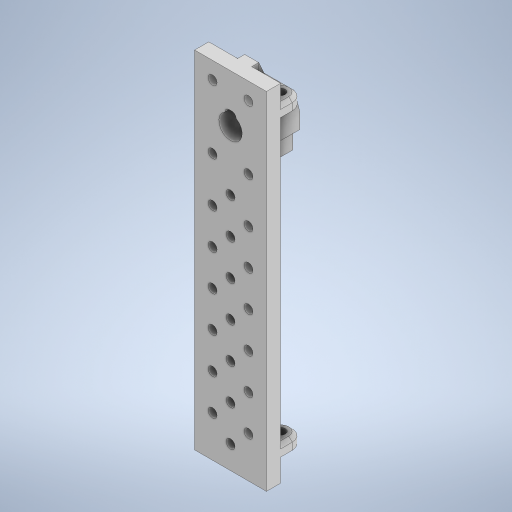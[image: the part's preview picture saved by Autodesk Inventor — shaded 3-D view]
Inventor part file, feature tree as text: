
AUTODESK INVENTOR PART (.ipt)
format: ipt  version: 2024 (Build 280153000, 153)  size: 1,184,256 bytes
history: native  units: mm
features: projected_geometry x30, extrude x22, sketch x18, plane x4, mirror x2, other x2, chamfer x1, loft x1
ambient origin geometry x8: Origin, YZ Plane, XZ Plane, XY Plane, X Axis, Y Axis, Z Axis, Center Point
bodies: Solid1 (feature_tree)
feature tree (80):
  extrude  "Extrusion1"  Depth=10.0mm
  extrude  "Extrusion2"  Depth=16.002mm
  extrude  "Extrusion3"  Depth=16.002mm
  plane  "Work Plane5"
  mirror  "Mirror1"
  extrude  "Extrusion4"  Depth=5.5118mm
  extrude  "Extrusion22"  Depth=2.9972mm
  extrude  "Extrusion23"  Depth=8.001mm
  extrude  "Extrusion24"  Depth=152.5mm
  extrude  "Extrusion14"  Depth=215.0mm
  plane  "Work Plane2"
  extrude  "Extrusion25"  Depth=8.25mm
  chamfer  "Chamfer1"  Distance=1.0mm
  plane  "Work Plane3"
  loft  "Loft6"
  extrude  "Extrusion27"  Depth=10.0mm
  extrude  "Extrusion28"  Depth=10.0mm
  extrude  "Extrusion29"  Depth=10.0mm
  plane  "Work Plane4"
  extrude  "Extrusion30"  Depth=10.0mm
  extrude  "Extrusion31"  Depth=10.0mm
  extrude  "Extrusion32"  Depth=10.0mm
  extrude  "Extrusion33"  Depth=10.0mm
  extrude  "Extrusion34"  Depth=10.0mm
  mirror  "Mirror2"
  extrude  "Extrusion35"  Depth=10.0mm
  extrude  "Extrusion36"  Depth=10.0mm
  extrude  "Extrusion37"  Depth=10.0mm
  sketch  "Sketch40"  dims[d25=1.0mm]
  extrude  "Extrusion38"  Depth=10.0mm
  extrude  "Extrusion39"  Depth=3.0mm
  sketch  "Sketch1"  dims[d0=5.0mm d1=10.0mm]
  projected_geometry  "Projected Loop1"
  projected_geometry  "Projected Loop2"
  projected_geometry  "Projected Loop3"
  projected_geometry  "Projected Loop17"
  sketch  "Sketch23"  dims[d2=122.8852mm d3=16.002mm]
  projected_geometry  "Projected Loop30"
  sketch  "Sketch24"  dims[d4=2.9972mm d5=16.002mm]
  projected_geometry  "Projected Loop31"
  sketch  "Sketch25"  dims[d6=11.938mm d7=5.5118mm]
  projected_geometry  "Projected Loop32"
  sketch  "Sketch26"  dims[d8=5.0038mm d9=2.9972mm]
  projected_geometry  "Projected Loop33"
  other  "Edges11"
  other  "Edges12"
  sketch  "Sketch29"  dims[d10=6.096mm d11=8.001mm]
  projected_geometry  "Projected Loop41"
  projected_geometry  "Projected Loop42"
  projected_geometry  "Projected Loop43"
  projected_geometry  "Projected Loop44"
  projected_geometry  "Projected Loop45"
  projected_geometry  "Projected Loop46"
  sketch  "Sketch30"  dims[d12=6.5mm d13=152.5mm]
  projected_geometry  "Projected Loop47"
  sketch  "Sketch31"  dims[d14=60.0mm d15=215.0mm]
  projected_geometry  "Projected Loop48"
  sketch  "Sketch32"  dims[d16=50.8mm d17=8.25mm]
  projected_geometry  "Projected Loop49"
  sketch  "Sketch33"  dims[d18=16.5mm]
  sketch  "Sketch34"  dims[d19=25.4mm]
  projected_geometry  "Projected Loop50"
  sketch  "Sketch35"  dims[d20=6.35mm]
  projected_geometry  "Projected Loop51"
  sketch  "Sketch36"  dims[d21=127.8852mm]
  projected_geometry  "Projected Loop52"
  sketch  "Sketch37"  dims[d22=10.0076mm]
  projected_geometry  "Projected Loop53"
  projected_geometry  "Projected Loop54"
  sketch  "Sketch38"  dims[d23=20.0mm]
  projected_geometry  "Projected Loop55"
  projected_geometry  "Projected Loop56"
  projected_geometry  "Projected Loop57"
  sketch  "Sketch39"  dims[d24=1.0mm]
  projected_geometry  "Projected Loop58"
  projected_geometry  "Projected Loop59"
  projected_geometry  "Projected Loop60"
  sketch  "Sketch41"  dims[d26=1.0mm d27=1.0mm d28=1.0mm d29=1.0mm d30=1.0mm d31=1.0mm d32=1.0mm d33=1.0mm d34=1.0mm d35=1.0mm d36=1.0mm d37=1.0mm d38=1.0mm d39=1.0mm d40=1.0mm d41=3.0mm d42=3.0mm d43=3.0mm d44=3.0mm d45=3.0mm d46=3.0mm d47=3.0mm d48=3.0mm d49=3.0mm d50=3.0mm d51=3.0mm d52=3.0mm d53=3.0mm d54=3.0mm d55=3.0mm d56=3.0mm d57=3.0mm d58=3.0mm d59=3.0mm d60=3.0mm d61=3.0mm d62=3.0mm d63=3.0mm d64=3.0mm d65=3.0mm d66=3.0mm d67=3.0mm d68=3.0mm d69=3.0mm d70=3.0mm d71=3.0mm d72=3.0mm d73=3.0mm d74=3.0mm d75=3.0mm d76=3.0mm d77=3.0mm d78=3.0mm d79=3.0mm d80=3.0mm d81=3.0mm d82=25.4mm d83=50.8mm d84=245.0mm d86=25.4mm d88=12.7mm d89=12.7mm d90=6.35mm d91=6.35mm d92=12.7mm d93=12.7mm d94=45.0deg d95=45.0deg d96=6.35mm d97=120.0mm d99=25.4mm d100=10.0mm d102=10.0mm d104=10.0mm d105=0.0mm d106=10.0mm d107=13.5128mm d108=10.0mm d109=13.5128mm d110=16.5mm d111=0.0mm d112=16.5mm d113=8.25mm d114=8.25mm d115=16.5mm d116=16.5mm d117=8.25mm d118=6.5mm d119=25.4mm d120=215.0mm d121=0.0mm d122=10.0076mm d123=16.096mm d124=8.048mm d125=182.5mm d126=26.002mm d127=0.0mm d186=50.8mm d187=10.0mm d188=30.4mm d189=0.0mm d190=10.0mm d191=5.0mm d192=0.0mm d196=2.5mm d197=2.0mm d198=45.0deg d236=0.0mm d237=16.096mm d238=26.002mm d239=6.096mm d240=8.001mm d241=6.096mm d242=8.001mm d243=17.0015mm d244=11.096mm d245=0.0mm d246=0.0mm d247=1.0mm d248=0.0mm d249=1.0mm d250=0.0mm d251=3.048mm d252=2.9972mm d257=25.76mm d258=0.0mm d259=0.0mm d260=90.0deg d261=0.0mm d262=90.0deg d269=26.0mm d271=50.8mm d272=25.4mm d273=26.0mm d274=-122.5mm d275=36.0mm d276=0.0mm d277=16.5mm d278=26.0mm d279=26.0mm d280=13.0mm d281=13.0mm d282=13.0mm d283=0.0mm d284=16.5mm d285=16.5mm d286=12.0mm d287=0.0mm d288=0.0mm d290=15.0mm d291=7.5mm d292=13.0mm d293=0.0mm d294=6.0mm d295=3.0mm d296=11.324752mm d297=13.0mm d298=5.662376mm d299=5.663mm d300=0.0mm d301=0.0mm d303=11.0mm d304=-122.5mm d305=68.0mm d306=50.8mm d307=34.0mm d308=10.0mm d309=0.0mm d310=68.0mm d311=34.0mm d312=50.8mm d313=0.0mm d314=6.35mm d318=12.7mm d319=17.0mm d320=20.0mm d322=25.4mm d323=20.0mm d325=45.0mm d328=10.0mm d329=0.0mm d330=22.5mm d331=6.0mm d332=3.0mm d333=0.0mm d334=6.0mm d335=2.0mm d336=0.0mm d337=8.0mm d338=0.0mm d339=0.0mm d340=10.25mm d341=16.5mm d342=3.0mm d343=0.0mm d344=0.0mm d346=6.5mm d348=10.0mm d349=0.0mm d350=15.0mm d351=15.0deg d352=0.0mm d353=0.0mm d354=5.5mm d355=9.75mm d356=9.75mm d357=6.75mm d358=6.75mm d359=10.0mm d360=0.0mm d361=10.0mm d362=0.0mm d199=0.872665mm d216=0.5mm d217=0.872665mm d218=0.5mm d219=0.872665mm d228=0.5mm d229=0.872665mm d230=0.5mm d231=0.872665mm]
  projected_geometry  "Projected Loop61"
  projected_geometry  "Projected Loop62"
